# Revit family: - Acero Roman
name_source: partatom
category: Doors
revit_build: Autodesk Revit 2018 (Build: 20170223_1515(x64)
units: mm (PartAtom-declared; Revit-internal decimal feet)

## family parameters
Always vertical = Yes
Cut with Voids When Loaded = No
Host = Wall
OmniClass Number = 23.30.10.00
OmniClass Title = Doors
Room Calculation Point = No
Shared = No

## types (12) — shared parameters
Analytic Construction = <None>
Distancia a Cara Interior = 6 cm
Frame Projection Ext. = 2.5 cm
Frame Projection Int. = 2.5 cm
Frame Width = 7.5 cm
Function = Interior
Hojas = Simple de Abatir
Manilla = - Manilla
Material Hoja = - Acero
Material Marco = - Perfil Aluminio
Wall Closure = By host

## per-type parameters (varying)
| type | Alto | Ancho | Ancho Hoja | Height | Width |
| - 70 x 200 cm | 200 cm | 74 cm | 70 cm | 200 cm | 74 cm |
| - 75 x 200 cm | 200 cm | 79 cm | 75 cm | 200 cm | 79 cm |
| - 80 x 200 cm | 200 cm | 84 cm | 80 cm | 200 cm | 84 cm |
| - 85 x 200 cm | 200 cm | 89 cm | 85 cm | 200 cm | 89 cm |
| - 90 x 200 cm | 200 cm | 94 cm | 90 cm | 200 cm | 94 cm |
| -100 x 200 cm | 200 cm | 104 cm | 100 cm | 200 cm | 104 cm |
| - 70 x 210 cm | 210 cm | 74 cm | 70 cm | 210 cm | 74 cm |
| - 75 x 210 cm | 210 cm | 79 cm | 75 cm | 210 cm | 79 cm |
| - 80 x 210 cm | 210 cm | 84 cm | 80 cm | 210 cm | 84 cm |
| - 85 x 210 cm | 210 cm | 89 cm | 85 cm | 210 cm | 89 cm |
| - 90 x 210 cm | 210 cm | 94 cm | 90 cm | 210 cm | 94 cm |
| - 100 x 210 cm | 210 cm | 104 cm | 100 cm | 210 cm | 104 cm |

## geometry (parser evidence)
native form markers: Blend x2, Sweep x5
no freeform markers — native parametric forms only
